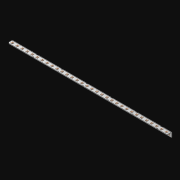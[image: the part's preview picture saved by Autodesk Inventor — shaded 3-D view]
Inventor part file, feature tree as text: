
AUTODESK INVENTOR PART (.ipt)
format: ipt  version: 2021 (Build 250183000, 183)  size: 847,360 bytes
history: native  units: in
note: dims shown in document units (in); Inventor stores cm internally (conversion verified against a paired STEP export)
features: extrude x65, other x64, sketch x3, pattern_linear x1, sheet_metal_op x1
ambient origin geometry x8: Origin, YZ Plane, XZ Plane, XY Plane, X Axis, Y Axis, Z Axis, Center Point
bodies: Solid1 (feature_tree)
feature tree (134):
  pattern_linear  "Rectangular Pattern1"  Spacing1=0.063in  [1 undecoded]
  extrude  "Extrusion1"  Depth=0.5in
  sketch  "Sketch1"  dims[d0=0.182in]
  other  "Srf1"
  sketch  "Sketch2"  dims[d1=0.063in d2=0.0in]
  other  "Srf2"
  other  "Srf3"
  other  "Srf5"
  other  "Srf7"
  other  "Srf9"
  other  "Srf11"
  other  "Srf13"
  other  "Srf15"
  other  "Srf17"
  other  "Srf19"
  other  "Srf21"
  other  "Srf23"
  other  "Srf25"
  other  "Srf27"
  other  "Srf29"
  other  "Srf31"
  other  "Srf33"
  other  "Srf35"
  other  "Srf37"
  other  "Srf39"
  other  "Srf41"
  other  "Srf43"
  other  "Srf45"
  other  "Srf47"
  other  "Srf49"
  other  "Srf51"
  other  "Srf53"
  other  "Srf55"
  other  "Srf57"
  other  "Srf59"
  other  "Srf61"
  other  "Srf63"
  other  "Srf4"
  other  "Srf6"
  other  "Srf8"
  other  "Srf10"
  other  "Srf12"
  other  "Srf14"
  other  "Srf16"
  other  "Srf18"
  other  "Srf20"
  other  "Srf22"
  other  "Srf24"
  other  "Srf26"
  other  "Srf28"
  other  "Srf30"
  other  "Srf32"
  other  "Srf34"
  other  "Srf36"
  other  "Srf38"
  other  "Srf40"
  other  "Srf42"
  other  "Srf44"
  other  "Srf46"
  other  "Srf48"
  other  "Srf50"
  other  "Srf52"
  other  "Srf54"
  other  "Srf56"
  other  "Srf58"
  other  "Srf60"
  other  "Srf62"
  other  "Srf64"
  sketch  "Sketch3"  dims[d3=0.182in d4=0.063in d5=0.0in d8=0.5in d9=1.5in d10=0.0in]
  sheet_metal_op  "Fold1"
  extrude  "ExtrusionSrf1"  Depth=0.5in TaperAngle=0.0deg
  extrude  "ExtrusionSrf2"  [1 undecoded]
  extrude  "ExtrusionSrf3"  [1 undecoded]
  extrude  "ExtrusionSrf4"  [1 undecoded]
  extrude  "ExtrusionSrf5"  [1 undecoded]
  extrude  "ExtrusionSrf6"  [1 undecoded]
  extrude  "ExtrusionSrf7"  [1 undecoded]
  extrude  "ExtrusionSrf8"  [1 undecoded]
  extrude  "ExtrusionSrf9"  [1 undecoded]
  extrude  "ExtrusionSrf10"  [1 undecoded]
  extrude  "ExtrusionSrf11"  [1 undecoded]
  extrude  "ExtrusionSrf12"  [1 undecoded]
  extrude  "ExtrusionSrf13"  [1 undecoded]
  extrude  "ExtrusionSrf14"  [1 undecoded]
  extrude  "ExtrusionSrf15"  [1 undecoded]
  extrude  "ExtrusionSrf16"  [1 undecoded]
  extrude  "ExtrusionSrf17"  [1 undecoded]
  extrude  "ExtrusionSrf18"  [1 undecoded]
  extrude  "ExtrusionSrf19"  [1 undecoded]
  extrude  "ExtrusionSrf20"  [1 undecoded]
  extrude  "ExtrusionSrf21"  [1 undecoded]
  extrude  "ExtrusionSrf22"  [1 undecoded]
  extrude  "ExtrusionSrf23"  [1 undecoded]
  extrude  "ExtrusionSrf24"  [1 undecoded]
  extrude  "ExtrusionSrf25"  [1 undecoded]
  extrude  "ExtrusionSrf26"  [1 undecoded]
  extrude  "ExtrusionSrf27"  [1 undecoded]
  extrude  "ExtrusionSrf28"  [1 undecoded]
  extrude  "ExtrusionSrf29"  [1 undecoded]
  extrude  "ExtrusionSrf30"  [1 undecoded]
  extrude  "ExtrusionSrf31"  [1 undecoded]
  extrude  "ExtrusionSrf32"  [1 undecoded]
  extrude  "ExtrusionSrf33"  [1 undecoded]
  extrude  "ExtrusionSrf37"  [1 undecoded]
  extrude  "ExtrusionSrf38"  [1 undecoded]
  extrude  "ExtrusionSrf39"  [1 undecoded]
  extrude  "ExtrusionSrf40"  [1 undecoded]
  extrude  "ExtrusionSrf41"  [1 undecoded]
  extrude  "ExtrusionSrf42"  [1 undecoded]
  extrude  "ExtrusionSrf43"  [1 undecoded]
  extrude  "ExtrusionSrf44"  [1 undecoded]
  extrude  "ExtrusionSrf45"  [1 undecoded]
  extrude  "ExtrusionSrf46"  [1 undecoded]
  extrude  "ExtrusionSrf47"  [1 undecoded]
  extrude  "ExtrusionSrf48"  [1 undecoded]
  extrude  "ExtrusionSrf49"  [1 undecoded]
  extrude  "ExtrusionSrf50"  [1 undecoded]
  extrude  "ExtrusionSrf51"  [1 undecoded]
  extrude  "ExtrusionSrf52"  [1 undecoded]
  extrude  "ExtrusionSrf53"  [1 undecoded]
  extrude  "ExtrusionSrf54"  [1 undecoded]
  extrude  "ExtrusionSrf55"  [1 undecoded]
  extrude  "ExtrusionSrf56"  [1 undecoded]
  extrude  "ExtrusionSrf57"  [1 undecoded]
  extrude  "ExtrusionSrf58"  [1 undecoded]
  extrude  "ExtrusionSrf59"  [1 undecoded]
  extrude  "ExtrusionSrf60"  [1 undecoded]
  extrude  "ExtrusionSrf61"  [1 undecoded]
  extrude  "ExtrusionSrf62"  [1 undecoded]
  extrude  "ExtrusionSrf63"  [1 undecoded]
  extrude  "ExtrusionSrf64"  [1 undecoded]
  extrude  "ExtrusionSrf65"  [1 undecoded]
  extrude  "ExtrusionSrf66"  [1 undecoded]
  extrude  "ExtrusionSrf67"  [1 undecoded]
note: 64 required parameter values undecoded (feature->parameter linkage not recoverable at this tier; creation-order binding heuristic only, values carry confidence <= 0.55)
